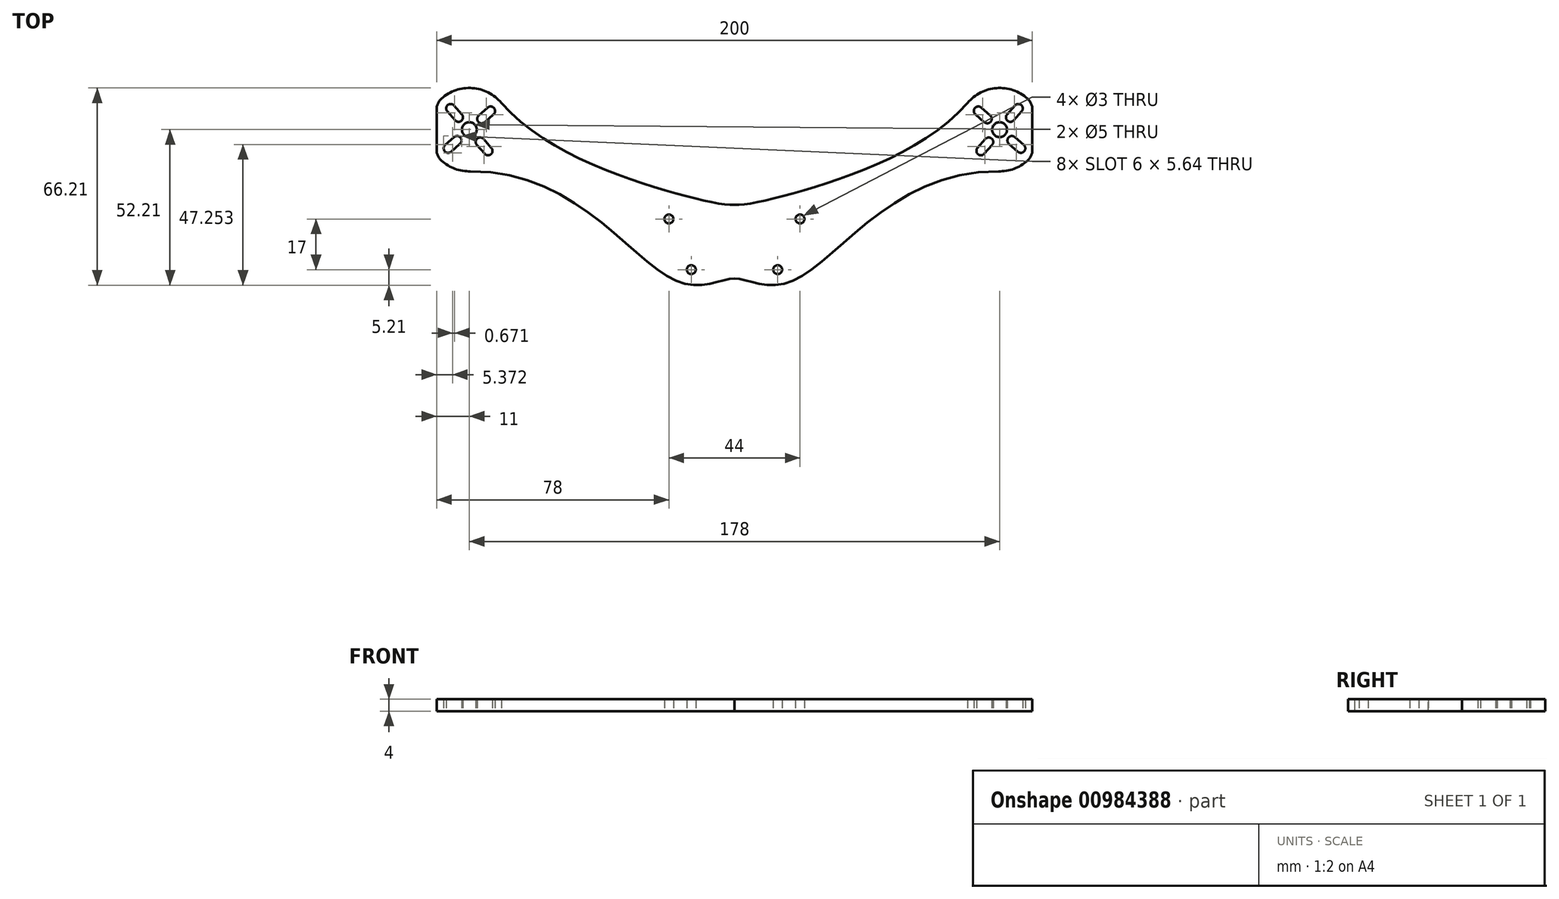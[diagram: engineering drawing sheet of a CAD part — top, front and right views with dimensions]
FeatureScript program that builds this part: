
annotation { "Feature Type Name" : "Feature", "Feature Type Description" : "" }
export const myFeature = defineFeature(function(context is Context, id is Id, definition is map)
    precondition{}
    {
        {
            var Q0;
            Q0=qCreatedBy(makeId("Top.planeOp"),FACE);
            var sketch = newSketch(context, id + "F0", { "sketchPlane" : qUnion([Q0])});
            skLineSegment(sketch, "E0.bottom", {"start": v(0, 0) * mm, "end": v(74.17, 0) * mm, "construction": true});
            skLineSegment(sketch, "E0.top", {"start": v(0, 30) * mm, "end": v(89, 30) * mm, "construction": true});
            skLineSegment(sketch, "E0.left", {"start": v(0, 0) * mm, "end": v(0, 30) * mm, "construction": true});
            skLineSegment(sketch, "E1", {"start": v(0, 0) * mm, "end": v(89, 30) * mm, "construction": true});
            skLineSegment(sketch, "E2", {"start": v(92.02, 27.34) * mm, "end": v(89, 30) * mm, "construction": true});
            skLineSegment(sketch, "E3.bottom", {"start": v(80.75, 37.27) * mm, "end": v(80.75, 37.27) * mm});
            skLineSegment(sketch, "E3.top", {"start": v(86, 32.64) * mm, "end": v(86, 32.64) * mm});
            skLineSegment(sketch, "E3.left", {"start": v(80.88, 35.15) * mm, "end": v(83.88, 32.5) * mm});
            skLineSegment(sketch, "E3.right", {"start": v(82.86, 37.4) * mm, "end": v(85.86, 34.76) * mm});
            skPoint(sketch, "E3.middle", {"position": v(83.37, 34.96) * mm});
            skPoint(sketch, "E4.visualSharp", {"position": v(81.74, 38.4) * mm});
            skArc(sketch, "E4.filletArc", {"start": v(82.86, 37.4) * mm, "mid": v(81.78, 37.78) * mm, "end": v(80.75, 37.27) * mm});
            skPoint(sketch, "E5.visualSharp", {"position": v(79.75, 36.14) * mm});
            skArc(sketch, "E5.filletArc", {"start": v(80.75, 37.27) * mm, "mid": v(80.37, 36.18) * mm, "end": v(80.88, 35.15) * mm});
            skPoint(sketch, "E6.visualSharp", {"position": v(85, 31.52) * mm});
            skArc(sketch, "E6.filletArc", {"start": v(83.88, 32.5) * mm, "mid": v(84.97, 32.14) * mm, "end": v(86, 32.64) * mm});
            skPoint(sketch, "E7.visualSharp", {"position": v(86.99, 33.77) * mm});
            skArc(sketch, "E7.filletArc", {"start": v(86, 32.64) * mm, "mid": v(86.37, 33.73) * mm, "end": v(85.86, 34.76) * mm});
            skLineSegment(sketch, "E8.1.0", {"start": v(83.85, 21.88) * mm, "end": v(86.5, 24.88) * mm});
            skArc(sketch, "E8.1.1", {"start": v(86.5, 24.88) * mm, "mid": v(86.86, 25.97) * mm, "end": v(86.36, 27) * mm});
            skArc(sketch, "E8.1.2", {"start": v(86.36, 27) * mm, "mid": v(85.27, 27.37) * mm, "end": v(84.24, 26.86) * mm});
            skLineSegment(sketch, "E8.1.3", {"start": v(81.6, 23.86) * mm, "end": v(84.24, 26.86) * mm});
            skArc(sketch, "E8.1.4", {"start": v(81.6, 23.86) * mm, "mid": v(81.22, 22.78) * mm, "end": v(81.73, 21.75) * mm});
            skArc(sketch, "E8.1.5", {"start": v(81.73, 21.75) * mm, "mid": v(82.82, 21.37) * mm, "end": v(83.85, 21.88) * mm});
            skLineSegment(sketch, "E8.2.0", {"start": v(97.12, 24.85) * mm, "end": v(94.12, 27.5) * mm});
            skArc(sketch, "E8.2.1", {"start": v(94.12, 27.5) * mm, "mid": v(93.03, 27.86) * mm, "end": v(92, 27.36) * mm});
            skArc(sketch, "E8.2.2", {"start": v(92, 27.36) * mm, "mid": v(91.63, 26.27) * mm, "end": v(92.14, 25.24) * mm});
            skLineSegment(sketch, "E8.2.3", {"start": v(95.14, 22.6) * mm, "end": v(92.14, 25.24) * mm});
            skArc(sketch, "E8.2.4", {"start": v(95.14, 22.6) * mm, "mid": v(96.22, 22.22) * mm, "end": v(97.25, 22.73) * mm});
            skArc(sketch, "E8.2.5", {"start": v(97.25, 22.73) * mm, "mid": v(97.63, 23.82) * mm, "end": v(97.12, 24.85) * mm});
            skLineSegment(sketch, "E8.3.0", {"start": v(94.15, 38.12) * mm, "end": v(91.5, 35.12) * mm});
            skArc(sketch, "E8.3.1", {"start": v(91.5, 35.12) * mm, "mid": v(91.14, 34.03) * mm, "end": v(91.64, 33) * mm});
            skArc(sketch, "E8.3.2", {"start": v(91.64, 33) * mm, "mid": v(92.73, 32.63) * mm, "end": v(93.76, 33.14) * mm});
            skLineSegment(sketch, "E8.3.3", {"start": v(96.4, 36.14) * mm, "end": v(93.76, 33.14) * mm});
            skArc(sketch, "E8.3.4", {"start": v(96.4, 36.14) * mm, "mid": v(96.78, 37.22) * mm, "end": v(96.27, 38.25) * mm});
            skArc(sketch, "E8.3.5", {"start": v(96.27, 38.25) * mm, "mid": v(95.18, 38.63) * mm, "end": v(94.15, 38.12) * mm});
            skPoint(sketch, "E8.center", {"position": v(89, 30) * mm});
            skCircle(sketch, "E9", {"center": v(89, 30) * mm, "radius": 2.5 * mm});
            skCircle(sketch, "E10", {"center": v(22, 0) * mm, "radius": 1.5 * mm});
            skCircle(sketch, "E11", {"center": v(14.5, -17) * mm, "radius": 1.5 * mm});
            skArc(sketch, "E12", {"start": v(98.33, 40.43) * mm, "mid": v(75, 30) * mm, "end": v(98.33, 19.57) * mm});
            skFitSpline(sketch, "E13", {"points": [v(0, -20) * mm, v(17.63, -21.5) * mm, v(88.6, 16) * mm], "startDerivative": vector(34.9, 1.77) * mm, "endDerivative": vector(159.91, -3.16) * mm});
            skFitSpline(sketch, "E14.MirrorCS", {"points": [v(0, -20) * mm, v(-17.63, -21.5) * mm, v(-88.6, 16) * mm], "startDerivative": vector(-34.9, 1.77) * mm, "endDerivative": vector(-159.91, -3.16) * mm});
            skCircle(sketch, "E15.MirrorC", {"center": v(-14.5, -17) * mm, "radius": 1.5 * mm});
            skCircle(sketch, "E16.MirrorC", {"center": v(-22, 0) * mm, "radius": 1.5 * mm});
            skArc(sketch, "E17.MirrorC", {"start": v(-98.33, 40.43) * mm, "mid": v(-75, 30) * mm, "end": v(-98.33, 19.57) * mm});
            skLineSegment(sketch, "E18.MirrorCS", {"start": v(-83.85, 21.88) * mm, "end": v(-86.5, 24.88) * mm});
            skLineSegment(sketch, "E19.MirrorCS", {"start": v(-81.6, 23.86) * mm, "end": v(-84.24, 26.86) * mm});
            skArc(sketch, "E20.MirrorCS", {"start": v(-81.6, 23.86) * mm, "mid": v(-81.22, 22.78) * mm, "end": v(-81.73, 21.75) * mm});
            skArc(sketch, "E21.MirrorCS", {"start": v(-81.73, 21.75) * mm, "mid": v(-82.82, 21.37) * mm, "end": v(-83.85, 21.88) * mm});
            skArc(sketch, "E22.MirrorCS", {"start": v(-86.5, 24.88) * mm, "mid": v(-86.86, 25.97) * mm, "end": v(-86.36, 27) * mm});
            skLineSegment(sketch, "E23.MirrorCS", {"start": v(-74.17, 0) * mm, "end": v(-89, 30) * mm, "construction": true});
            skArc(sketch, "E24.MirrorCS", {"start": v(-86.36, 27) * mm, "mid": v(-85.27, 27.37) * mm, "end": v(-84.24, 26.86) * mm});
            skLineSegment(sketch, "E25.MirrorCS", {"start": v(-95.14, 22.6) * mm, "end": v(-92.14, 25.24) * mm});
            skArc(sketch, "E26.MirrorCS", {"start": v(-92, 27.36) * mm, "mid": v(-91.63, 26.27) * mm, "end": v(-92.14, 25.24) * mm});
            skArc(sketch, "E27.MirrorCS", {"start": v(-95.14, 22.6) * mm, "mid": v(-96.22, 22.22) * mm, "end": v(-97.25, 22.73) * mm});
            skArc(sketch, "E28.MirrorCS", {"start": v(-97.25, 22.73) * mm, "mid": v(-97.63, 23.82) * mm, "end": v(-97.12, 24.85) * mm});
            skLineSegment(sketch, "E29.MirrorCS", {"start": v(-97.12, 24.85) * mm, "end": v(-94.12, 27.5) * mm});
            skArc(sketch, "E30.MirrorCS", {"start": v(-94.12, 27.5) * mm, "mid": v(-93.03, 27.86) * mm, "end": v(-92, 27.36) * mm});
            skLineSegment(sketch, "E31.MirrorCS", {"start": v(-96.4, 36.14) * mm, "end": v(-93.76, 33.14) * mm});
            skArc(sketch, "E32.MirrorCS", {"start": v(-96.4, 36.14) * mm, "mid": v(-96.78, 37.22) * mm, "end": v(-96.27, 38.25) * mm});
            skArc(sketch, "E33.MirrorCS", {"start": v(-96.27, 38.25) * mm, "mid": v(-95.18, 38.63) * mm, "end": v(-94.15, 38.12) * mm});
            skLineSegment(sketch, "E34.MirrorCS", {"start": v(-94.15, 38.12) * mm, "end": v(-91.5, 35.12) * mm});
            skArc(sketch, "E35.MirrorCS", {"start": v(-91.5, 35.12) * mm, "mid": v(-91.14, 34.03) * mm, "end": v(-91.64, 33) * mm});
            skArc(sketch, "E36.MirrorCS", {"start": v(-91.64, 33) * mm, "mid": v(-92.73, 32.63) * mm, "end": v(-93.76, 33.14) * mm});
            skLineSegment(sketch, "E37.MirrorCS", {"start": v(-80.88, 35.15) * mm, "end": v(-83.88, 32.5) * mm});
            skArc(sketch, "E38.MirrorCS", {"start": v(-80.75, 37.27) * mm, "mid": v(-80.37, 36.18) * mm, "end": v(-80.88, 35.15) * mm});
            skArc(sketch, "E39.MirrorCS", {"start": v(-82.86, 37.4) * mm, "mid": v(-81.78, 37.78) * mm, "end": v(-80.75, 37.27) * mm});
            skLineSegment(sketch, "E40.MirrorCS", {"start": v(-82.86, 37.4) * mm, "end": v(-85.86, 34.76) * mm});
            skArc(sketch, "E41.MirrorCS", {"start": v(-86, 32.64) * mm, "mid": v(-86.37, 33.73) * mm, "end": v(-85.86, 34.76) * mm});
            skArc(sketch, "E42.MirrorCS", {"start": v(-83.88, 32.5) * mm, "mid": v(-84.97, 32.14) * mm, "end": v(-86, 32.64) * mm});
            skCircle(sketch, "E43.MirrorC", {"center": v(-89, 30) * mm, "radius": 2.5 * mm});
            skFitSpline(sketch, "E44", {"points": [v(0, 4.75) * mm, v(21.35, 9.12) * mm, v(78.6, 39.37) * mm], "startDerivative": vector(30.65, -1.56) * mm, "endDerivative": vector(67.83, 78.8) * mm});
            skFitSpline(sketch, "E45.MirrorCS", {"points": [v(0, 4.75) * mm, v(-21.35, 9.12) * mm, v(-78.6, 39.37) * mm], "startDerivative": vector(-30.65, -1.56) * mm, "endDerivative": vector(-67.83, 78.8) * mm});
            skLineSegment(sketch, "E46", {"start": v(100, 36.7) * mm, "end": v(100, 23.3) * mm});
            skArc(sketch, "E47.filletArc", {"start": v(100, 36.7) * mm, "mid": v(99.56, 38.75) * mm, "end": v(98.33, 40.43) * mm});
            skArc(sketch, "E48.filletArc", {"start": v(98.33, 19.57) * mm, "mid": v(99.56, 21.25) * mm, "end": v(100, 23.3) * mm});
            skLineSegment(sketch, "E49.MirrorCS", {"start": v(-100, 36.7) * mm, "end": v(-100, 23.3) * mm});
            skArc(sketch, "E50.MirrorCS", {"start": v(-100, 36.7) * mm, "mid": v(-99.56, 38.75) * mm, "end": v(-98.33, 40.43) * mm});
            skArc(sketch, "E51.MirrorCS", {"start": v(-98.33, 19.57) * mm, "mid": v(-99.56, 21.25) * mm, "end": v(-100, 23.3) * mm});
            skSolve(sketch);
        }
        {
            var Q0;
            Q0 = qSketchRegion(id + "F0", true);
            extrude(context, id + "F1", {"entities" : qUnion([Q0]), "depth" : 4 * mm, "offsetDistance" : 25 * mm});
        }
    });
